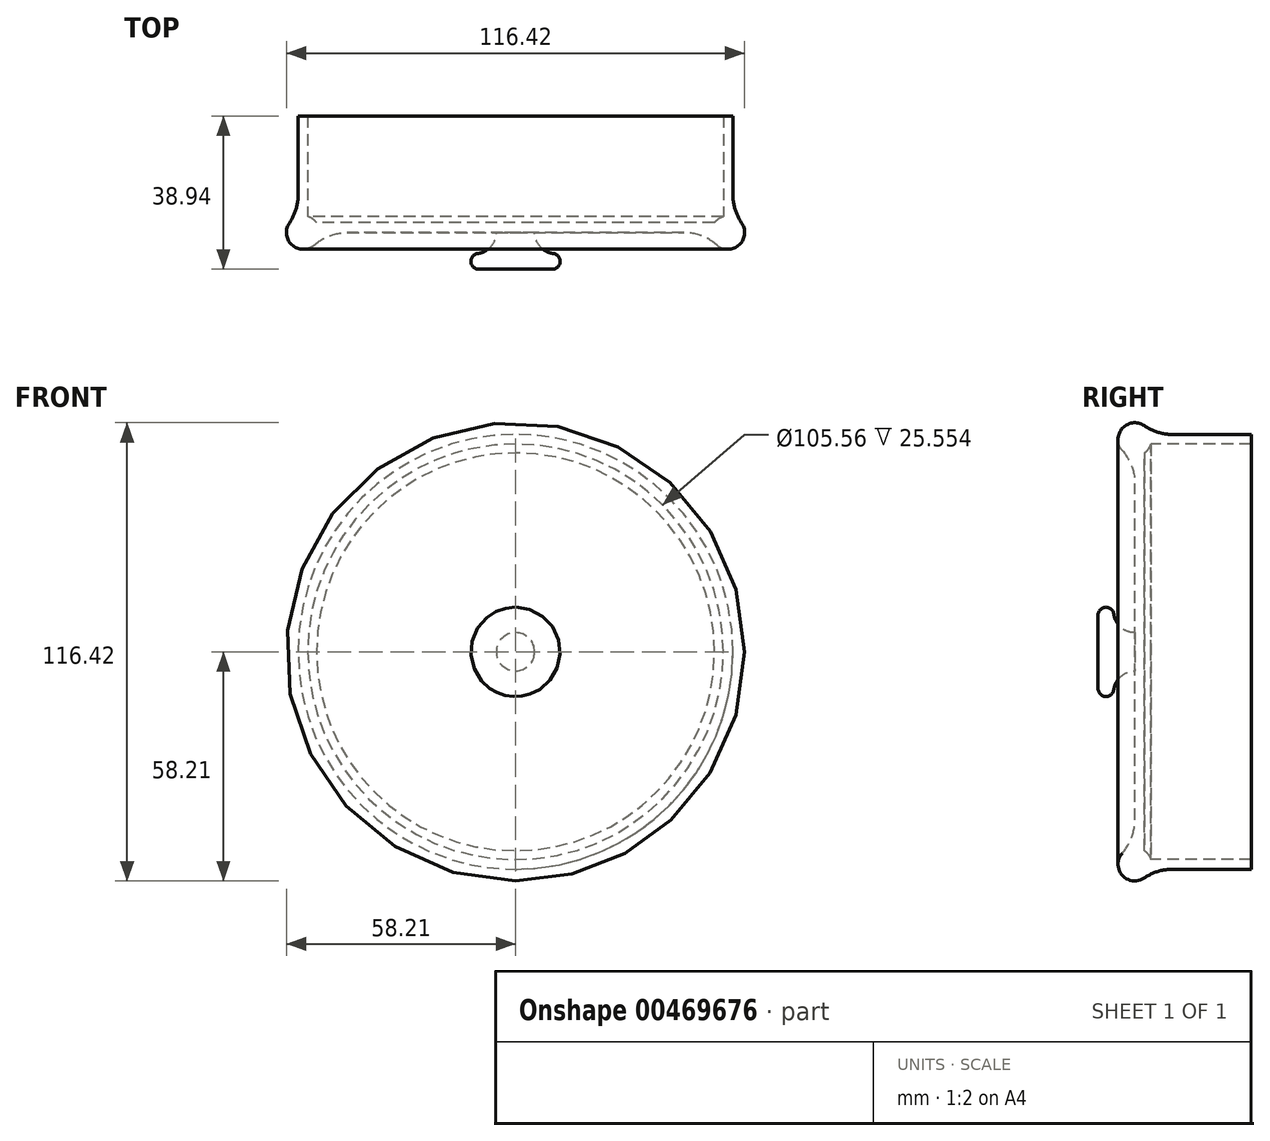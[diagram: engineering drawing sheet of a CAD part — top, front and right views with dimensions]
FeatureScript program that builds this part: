
annotation { "Feature Type Name" : "Feature", "Feature Type Description" : "" }
export const myFeature = defineFeature(function(context is Context, id is Id, definition is map)
    precondition{}
    {
        {
            var Q0;
            Q0=qCreatedBy(makeId("Front.planeOp"),FACE);
            var sketch = newSketch(context, id + "F0", { "sketchPlane" : qUnion([Q0])});
            skCircle(sketch, "E0", {"center": v(0, 0) * mm, "radius": 54.82 * mm});
            skSolve(sketch);
        }
        {
            var Q0;
            Q0=qCreatedBy(makeId("Top.planeOp"),FACE);
            var sketch = newSketch(context, id + "F1", { "sketchPlane" : qUnion([Q0])});
            skArc(sketch, "E1", {"start": v(52.78, 4.08) * mm, "mid": v(51.52, 3.48) * mm, "end": v(50.53, 2.5) * mm});
            skLineSegment(sketch, "E2.top", {"start": v(52.78, 29.63) * mm, "end": v(55.23, 29.63) * mm});
            skLineSegment(sketch, "E2.left", {"start": v(52.78, 4.08) * mm, "end": v(52.78, 29.63) * mm});
            skLineSegment(sketch, "E2.right", {"start": v(55.23, 4.05) * mm, "end": v(55.23, 29.63) * mm});
            skLineSegment(sketch, "E3.bottom", {"start": v(0, 0) * mm, "end": v(49.72, 0) * mm});
            skLineSegment(sketch, "E3.top", {"start": v(0, 2.5) * mm, "end": v(50.53, 2.5) * mm});
            skLineSegment(sketch, "E3.left", {"start": v(0, 0) * mm, "end": v(0, 2.5) * mm});
            skArc(sketch, "E4.trimOffspring", {"start": v(49.72, 0) * mm, "mid": v(56.48, -3.42) * mm, "end": v(55.23, 4.05) * mm});
            skSolve(sketch);
        }
        {
            var Q0;
            Q0 = qSketchRegion(id + "F1", true);
            var Q1;
            Q1=sQuery(id+"F0.wireOp",EDGE,"E0");
            sweep(context, id + "F2", {"profiles" : qUnion([Q0]), "path" : qUnion([Q1])});
        }
        {
            var Q0;
            Q0=makeQuery(id+"F2.opSweep","SWEPT_EDGE",EDGE,{"disambiguationData":[OSD([sQuery(id+"F0.wireOp",EDGE,"E0"),sQuery(id+"F1.wireOp",EDGE,"E3.bottom"),sQuery(id+"F1.wireOp",EDGE,"E4.trimOffspring")])]});
            var Q1;
            Q1=makeQuery(id+"F2.opSweep","SWEPT_EDGE",EDGE,{"disambiguationData":[OSD([sQuery(id+"F0.wireOp",EDGE,"E0"),sQuery(id+"F1.wireOp",EDGE,"E2.right"),sQuery(id+"F1.wireOp",EDGE,"E4.trimOffspring")])]});
            fillet(context, id + "F3", {"entities" : qUnion([Q0, Q1]), "radius" : 12.7 * mm, "tangentPropagation" : true, "allowEdgeOverflow" : false});
        }
        {
            var Q0;
            Q0=qCreatedBy(makeId("Top.planeOp"),FACE);
            var sketch = newSketch(context, id + "F4", { "sketchPlane" : qUnion([Q0])});
            skLineSegment(sketch, "E5.0", {"start": v(4.86, 0) * mm, "end": v(0, 0) * mm});
            skLineSegment(sketch, "E6", {"start": v(0, 0) * mm, "end": v(0, -9.31) * mm});
            skLineSegment(sketch, "E7", {"start": v(0, -9.31) * mm, "end": v(9.34, -9.31) * mm});
            skArc(sketch, "E8", {"start": v(9.34, -9.31) * mm, "mid": v(11.34, -7.45) * mm, "end": v(9.6, -5.33) * mm});
            skArc(sketch, "E9", {"start": v(9.6, -5.33) * mm, "mid": v(6.24, -3.55) * mm, "end": v(4.86, 0) * mm});
            skPoint(sketch, "E10.orphan", {"position": v(-42.74, 0) * mm});
            skPoint(sketch, "E11.orphan", {"position": v(42.74, 0) * mm});
            skSolve(sketch);
        }
        {
            var Q0;
            Q0 = qSketchRegion(id + "F4", true);
            var Q1;
            Q1=sQuery(id+"F4.wireOp",EDGE,"E6");
            revolve(context, id + "F5", {"operationType" : NewBodyOperationType.ADD, "entities" : qUnion([Q0]), "axis" : qUnion([Q1]), "revolveType" : RevolveType.FULL});
        }
    });
